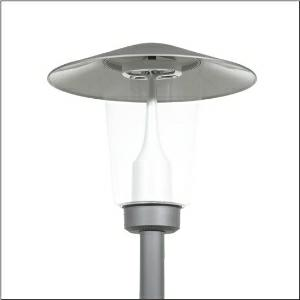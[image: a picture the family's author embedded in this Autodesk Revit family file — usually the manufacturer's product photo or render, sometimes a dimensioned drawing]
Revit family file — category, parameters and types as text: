
# Revit family: pilzleuchte_iq___st1_2a_5xa5235ef14h_b780
name_source: partatom
category: Lighting Fixtures
units: mm (PartAtom-declared; Revit-internal decimal feet)

## family parameters
Cut with Voids When Loaded = No
Host = Face
Light Source = No
Part Type = Normal
Room Calculation Point = No
Round Connector Dimension = Use Diameter
Shared = No

## types (1)
- --- (1 x LED, 1550 lm, 10.5 W, 3000K)
    Apparent Load = 11 VA
    CIE Flux Codes = 24 61 93 98 100
    Color Rendering = 70
    Color Temperature = 3000K
    Default Elevation = 1800 mm
    Description = Mushroom Luminaire iQ, mast luminaire, Module 540 iQ-SR, primary light control with 3 zone facetted reflector, of plastic, silver coated, highly specular, structured, primary optical cover: cover, of PMMA, transparent, light distribution: ST1.2a, light emission: direct distribution, primary light characteristic: asymmetric, installation type: post-top, LED, High Power LED, rated luminous flux: 1.550lm, luminous efficacy: 148lm/W, light colour: 730, colour temperature: 3000K, control gear: iQ Street-Remote, control: Auto-Match, Temp-Guard, Lumen-Switch, Night-Set, Smart-Wire, Light-Fading, Desk-Remote (wireless, voltage-free reading and setting of iQ features in the workshop via application-optimized NFC function/RFID function), optimised constant luminous flux control (CLO 2.0), Street-Remote, pre-setting: logarithmic dimming characteristic, with terminal, 6-pole, max. 2.5mm², mains connection: 230..240V, AC, 50/60Hz, start of lifetime: 11W, end of service life: 11W, reduction: 5W, luminaire housing, upper part, of glass-fibre reinforced polyester, coated, Siteco® metallic grey (DB 702S), diameter: 650mm, height: 586mm, spigot size: d x l = 76 x 70mm (post-top) | with reducer (optional accessory) 60 x 70mm, mounting height: 3..5m, post-top mast mounting element, of diecast aluminium, coated, Siteco® metallic grey (DB 702S), Module 540 iQ-SR, traffic white (RAL 9016), equipment: standard, protection rating (complete): IP65, insulation class (complete): insulation class II (safety insulation), certification: CE, ENEC, VDE, packaging unit: 1 piece

Light Distribution: ST1.2a
    Height = 586 mm
    Lamp = 1 x LED
    Lamp Light Flux = 1550 lm
    Lamp Power = 10.5 W
    Lamp count = 1
    Length = 650 mm
    Luminous efficacy = 148 lm/W
    Manufacturer = Siteco
    ModVariant = No
    Model = 5XA5235EF14H
    Number of Poles = 1
    OnlyDefault = Yes
    Power Factor = 1
    Product Name = Pilzleuchte iQ | ST1.2a
    Product group = mast luminaire | pylon top
    ProductGroupID = 6100
    Protection Class = Protection class II
    Protection Degree = IP 65
    RLX_Detail_Level = 1
    RLX_Emergency_Light_Flux = 0 lm
    RLX_Emergency_Type = 0
    RLX_Emergency_Type_DB = No
    RlxData = <blob elided: 122945 chars, md5=19ea19f2>
    Socket = socket
    Standby Power = 0 W
    System Light Flux = 1550 lm
    System Power = 11 W
    Type Comments = factory setting: luminous flux: 100 % | dim-lin: 254 | 419 mA
    Type Image = l_1006077.jpg
    URL = http://relux.com
    VarID = @adj_160243
    Voltage = 0 V
    Weight = 0.00 kg
    Width = 0 mm  [stored 0 ft]

note: [stored X ft] marks values corroborated as IEEE doubles in the binary element streams (Revit-internal decimal feet)

## geometry (parser evidence)
native form markers: Blend x4, Sweep x8
no freeform markers — native parametric forms only
